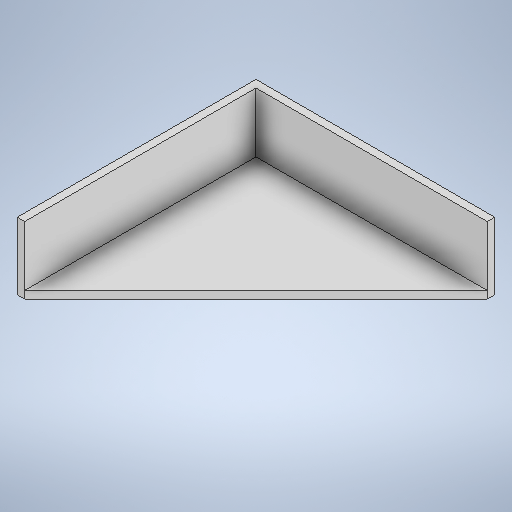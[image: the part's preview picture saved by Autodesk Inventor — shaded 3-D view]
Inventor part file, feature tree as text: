
AUTODESK INVENTOR PART (.ipt)
format: ipt  version: 2025.1 (Build 291241020, 241B)  size: 228,352 bytes
history: native  units: in
note: dims shown in document units (in); Inventor stores cm internally (conversion verified against a paired STEP export)
features: extrude x2, sketch x2
ambient origin geometry x8: Origin, YZ Plane, XZ Plane, XY Plane, X Axis, Y Axis, Z Axis, Center Point
bodies: Solid1 (feature_tree)
feature tree (4):
  extrude  "Extrusion1"  Depth=0.125in
  extrude  "Extrusion2"  Depth=4.0in
  sketch  "Sketch1"  dims[d0=4.0in d1=0.125in]
  sketch  "Sketch2"  dims[d2=0.125in d3=4.0in d4=1.125in d5=0.0in d6=0.125in d7=0.0in]
